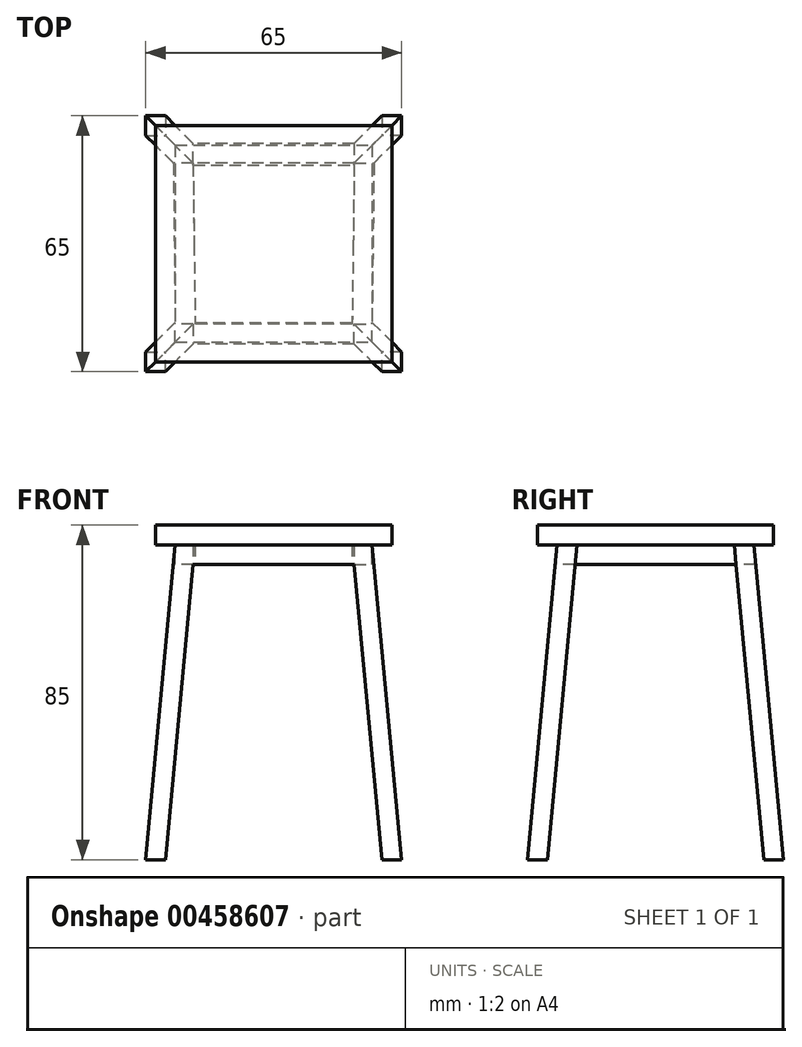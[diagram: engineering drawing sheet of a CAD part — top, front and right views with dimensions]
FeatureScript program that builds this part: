
annotation { "Feature Type Name" : "Feature", "Feature Type Description" : "" }
export const myFeature = defineFeature(function(context is Context, id is Id, definition is map)
    precondition{}
    {
        {
            var Q0;
            Q0=qCreatedBy(makeId("Top.planeOp"),FACE);
            var sketch = newSketch(context, id + "F0", { "sketchPlane" : qUnion([Q0])});
            skPoint(sketch, "E0.end.orphan", {"position": v(21.97, -20.2) * mm});
            skPoint(sketch, "E1.end.orphan", {"position": v(20, 29.8) * mm});
            skPoint(sketch, "E1.start.orphan", {"position": v(-30, 30) * mm});
            skLineSegment(sketch, "E2.bottom", {"start": v(-30, 30) * mm, "end": v(30, 30) * mm});
            skLineSegment(sketch, "E2.top", {"start": v(-30, -30) * mm, "end": v(30, -30) * mm});
            skLineSegment(sketch, "E2.left", {"start": v(-30, 30) * mm, "end": v(-30, -30) * mm});
            skLineSegment(sketch, "E2.right", {"start": v(30, 30) * mm, "end": v(30, -30) * mm});
            skPoint(sketch, "E2.middle", {"position": v(0, 0) * mm});
            skSolve(sketch);
        }
        {
            var Q0;
            Q0 = qSketchRegion(id + "F0", true);
            extrude(context, id + "F1", {"entities" : qUnion([Q0]), "depth" : 5 * mm});
        }
        {
            var Q0;
            Q0=makeQuery(id+"F1.opExtrude","CAP_FACE",FACE,{"disambiguationData":[OSD([sQuery(id+"F0.wireOp",EDGE,"E2.bottom"),sQuery(id+"F0.wireOp",EDGE,"E2.top"),sQuery(id+"F0.wireOp",EDGE,"E2.left"),sQuery(id+"F0.wireOp",EDGE,"E2.right")])],"isStart":true});
            var sketch = newSketch(context, id + "F2", { "sketchPlane" : qUnion([Q0])});
            skLineSegment(sketch, "E3.bottom", {"start": v(-25, 25) * mm, "end": v(25, 25) * mm, "construction": true});
            skLineSegment(sketch, "E3.top", {"start": v(-25, -25) * mm, "end": v(25, -25) * mm, "construction": true});
            skLineSegment(sketch, "E3.left", {"start": v(-25, 25) * mm, "end": v(-25, -25) * mm, "construction": true});
            skLineSegment(sketch, "E3.right", {"start": v(25, 25) * mm, "end": v(25, -25) * mm, "construction": true});
            skPoint(sketch, "E3.middle", {"position": v(0, 0) * mm});
            skLineSegment(sketch, "E4.bottom", {"start": v(-25, 25) * mm, "end": v(-20, 25) * mm});
            skLineSegment(sketch, "E4.top", {"start": v(-25, 20) * mm, "end": v(-20, 20) * mm});
            skLineSegment(sketch, "E4.left", {"start": v(-25, 25) * mm, "end": v(-25, 20) * mm});
            skLineSegment(sketch, "E4.right", {"start": v(-20, 25) * mm, "end": v(-20, 20) * mm});
            skSolve(sketch);
        }
        {
            var Q0;
            Q0=makeQuery(id+"F2.imprint","IMPRINT",FACE,{"disambiguationData":[TD([[makeQuery(id+"F2.imprint","IMPRINT",EDGE,{"derivedFrom":sQuery(id+"F2.wireOp",EDGE,"E4.bottom")}),1.0]])]});
            cPlane(context, id + "F3", {"entities" : qUnion([Q0]), "cplaneType" : CPlaneType.OFFSET, "offset" : 80 * mm, "width" : 150 * mm, "height" : 150 * mm});
        }
        {
            var Q0;
            Q0=qCreatedBy(id+"F3.planeOp",FACE);
            var sketch = newSketch(context, id + "F4", { "sketchPlane" : qUnion([Q0])});
            skLineSegment(sketch, "E5.bottom", {"start": v(-32.5, 32.5) * mm, "end": v(32.5, 32.5) * mm, "construction": true});
            skLineSegment(sketch, "E5.top", {"start": v(-32.5, -32.5) * mm, "end": v(32.5, -32.5) * mm, "construction": true});
            skLineSegment(sketch, "E5.left", {"start": v(-32.5, 32.5) * mm, "end": v(-32.5, -32.5) * mm, "construction": true});
            skLineSegment(sketch, "E5.right", {"start": v(32.5, 32.5) * mm, "end": v(32.5, -32.5) * mm, "construction": true});
            skPoint(sketch, "E5.middle", {"position": v(0, 0) * mm});
            skLineSegment(sketch, "E6.bottom", {"start": v(-32.5, 32.5) * mm, "end": v(-27.5, 32.5) * mm});
            skLineSegment(sketch, "E6.top", {"start": v(-32.5, 27.5) * mm, "end": v(-27.5, 27.5) * mm});
            skLineSegment(sketch, "E6.left", {"start": v(-32.5, 32.5) * mm, "end": v(-32.5, 27.5) * mm});
            skLineSegment(sketch, "E6.right", {"start": v(-27.5, 32.5) * mm, "end": v(-27.5, 27.5) * mm});
            skSolve(sketch);
        }
        {
            var Q1;
            Q1=makeQuery(id+"F2.imprint","IMPRINT",FACE,{"disambiguationData":[TD([[makeQuery(id+"F2.imprint","IMPRINT",EDGE,{"derivedFrom":sQuery(id+"F2.wireOp",EDGE,"E4.bottom")}),-1.0]])]});
            var Q2;
            Q2=makeQuery(id+"F4.imprint","IMPRINT",FACE,{"disambiguationData":[TD([[makeQuery(id+"F4.imprint","IMPRINT",EDGE,{"derivedFrom":sQuery(id+"F4.wireOp",EDGE,"E6.bottom")}),-1.0]])]});
            loft(context, id + "F5", {"sheetProfilesArray" : [{ "sheetProfileEntities" : qUnion([Q1]) }, { "sheetProfileEntities" : qUnion([Q2]) }]});
        }
        {
            var Q0;
            Q0=makeQuery(id+"F5.opLoft","SWEPT_BODY",BODY,{"disambiguationData":[OSD([makeQuery(id+"F2.imprint","IMPRINT",FACE,{"disambiguationData":[TD([[makeQuery(id+"F2.imprint","IMPRINT",EDGE,{"derivedFrom":sQuery(id+"F2.wireOp",EDGE,"E4.bottom")}),-1.0]])]}),makeQuery(id+"F4.imprint","IMPRINT",FACE,{"disambiguationData":[TD([[makeQuery(id+"F4.imprint","IMPRINT",EDGE,{"derivedFrom":sQuery(id+"F4.wireOp",EDGE,"E6.bottom")}),-1.0]])]})])]});
            var Q1;
            Q1=qCreatedBy(makeId("Right.planeOp"),FACE);
            mirror(context, id + "F6", {"entities" : qUnion([Q0]), "mirrorPlane" : qUnion([Q1])});
        }
        {
            var Q0;
            Q0=makeQuery(id+"F5.opLoft","SWEPT_BODY",BODY,{"disambiguationData":[OSD([makeQuery(id+"F2.imprint","IMPRINT",FACE,{"disambiguationData":[TD([[makeQuery(id+"F2.imprint","IMPRINT",EDGE,{"derivedFrom":sQuery(id+"F2.wireOp",EDGE,"E4.bottom")}),-1.0]])]}),makeQuery(id+"F4.imprint","IMPRINT",FACE,{"disambiguationData":[TD([[makeQuery(id+"F4.imprint","IMPRINT",EDGE,{"derivedFrom":sQuery(id+"F4.wireOp",EDGE,"E6.bottom")}),-1.0]])]})])]});
            var Q1;
            Q1=makeQuery(id+"F6.opPattern","COPY",BODY,{"derivedFrom":makeQuery(id+"F5.opLoft","SWEPT_BODY",BODY,{"disambiguationData":[OSD([makeQuery(id+"F2.imprint","IMPRINT",FACE,{"disambiguationData":[TD([[makeQuery(id+"F2.imprint","IMPRINT",EDGE,{"derivedFrom":sQuery(id+"F2.wireOp",EDGE,"E4.bottom")}),-1.0]])]}),makeQuery(id+"F4.imprint","IMPRINT",FACE,{"disambiguationData":[TD([[makeQuery(id+"F4.imprint","IMPRINT",EDGE,{"derivedFrom":sQuery(id+"F4.wireOp",EDGE,"E6.bottom")}),-1.0]])]})])]}),"instanceName":"1"});
            var Q2;
            Q2=qCreatedBy(makeId("Front.planeOp"),FACE);
            mirror(context, id + "F7", {"operationType" : NewBodyOperationType.ADD, "entities" : qUnion([Q0, Q1]), "mirrorPlane" : qUnion([Q2])});
        }
        {
            var Q0;
            Q0=makeQuery(id+"F5.opLoft","SWEPT_FACE",FACE,{"disambiguationData":[OSD([sQuery(id+"F2.wireOp",EDGE,"E4.bottom"),sQuery(id+"F2.wireOp",EDGE,"E4.top"),sQuery(id+"F2.wireOp",EDGE,"E4.right"),sQuery(id+"F4.wireOp",EDGE,"E6.bottom"),sQuery(id+"F4.wireOp",EDGE,"E6.top"),sQuery(id+"F4.wireOp",EDGE,"E6.right")])]});
            var sketch = newSketch(context, id + "F8", { "sketchPlane" : qUnion([Q0])});
            skLineSegment(sketch, "E7", {"start": v(-25, -1.87) * mm, "end": v(-20, -1.87) * mm});
            skLineSegment(sketch, "E8", {"start": v(-20, -1.87) * mm, "end": v(-20.46, -6.85) * mm});
            skLineSegment(sketch, "E9", {"start": v(-20.46, -6.85) * mm, "end": v(-25.46, -6.85) * mm});
            skLineSegment(sketch, "E10", {"start": v(-25.46, -6.85) * mm, "end": v(-25, -1.87) * mm});
            skSolve(sketch);
        }
        {
            var Q0;
            Q0=makeQuery(id+"F6.opPattern","COPY",FACE,{"derivedFrom":makeQuery(id+"F5.opLoft","SWEPT_FACE",FACE,{"disambiguationData":[OSD([sQuery(id+"F2.wireOp",EDGE,"E4.bottom"),sQuery(id+"F2.wireOp",EDGE,"E4.top"),sQuery(id+"F2.wireOp",EDGE,"E4.right"),sQuery(id+"F4.wireOp",EDGE,"E6.bottom"),sQuery(id+"F4.wireOp",EDGE,"E6.top"),sQuery(id+"F4.wireOp",EDGE,"E6.right")])]}),"instanceName":"1"});
            var sketch = newSketch(context, id + "F9", { "sketchPlane" : qUnion([Q0])});
            skLineSegment(sketch, "E11", {"start": v(20, -1.87) * mm, "end": v(25, -1.87) * mm});
            skLineSegment(sketch, "E12", {"start": v(25, -1.87) * mm, "end": v(25.46, -6.85) * mm});
            skLineSegment(sketch, "E13", {"start": v(25.46, -6.85) * mm, "end": v(20.46, -6.85) * mm});
            skLineSegment(sketch, "E14", {"start": v(20.46, -6.85) * mm, "end": v(20, -1.87) * mm});
            skSolve(sketch);
        }
        {
            var Q1;
            Q1=makeQuery(id+"F9.imprint","IMPRINT",FACE,{"disambiguationData":[TD([[makeQuery(id+"F9.imprint","IMPRINT",EDGE,{"derivedFrom":sQuery(id+"F9.wireOp",EDGE,"E11")}),-1.0]])]});
            var Q2;
            Q2=makeQuery(id+"F8.imprint","IMPRINT",FACE,{"disambiguationData":[TD([[makeQuery(id+"F8.imprint","IMPRINT",EDGE,{"derivedFrom":sQuery(id+"F8.wireOp",EDGE,"E7")}),1.0]])]});
            loft(context, id + "F10", {"sheetProfilesArray" : [{ "sheetProfileEntities" : qUnion([Q1]) }, { "sheetProfileEntities" : qUnion([Q2]) }]});
        }
        {
            var Q0;
            Q0=makeQuery(id+"F10.opLoft","SWEPT_BODY",BODY,{"disambiguationData":[OSD([makeQuery(id+"F8.imprint","IMPRINT",FACE,{"disambiguationData":[TD([[makeQuery(id+"F8.imprint","IMPRINT",EDGE,{"derivedFrom":sQuery(id+"F8.wireOp",EDGE,"E7")}),1.0]])]}),makeQuery(id+"F9.imprint","IMPRINT",FACE,{"disambiguationData":[TD([[makeQuery(id+"F9.imprint","IMPRINT",EDGE,{"derivedFrom":sQuery(id+"F9.wireOp",EDGE,"E11")}),-1.0]])]})])]});
            var Q1;
            Q1=qCreatedBy(makeId("Front.planeOp"),FACE);
            mirror(context, id + "F11", {"operationType" : NewBodyOperationType.ADD, "entities" : qUnion([Q0]), "mirrorPlane" : qUnion([Q1])});
        }
        {
            var Q0;
            {var subQ0=sQuery(id+"F4.wireOp",EDGE,"E6.right");var subQ1=sQuery(id+"F4.wireOp",EDGE,"E6.top");var subQ2=sQuery(id+"F2.wireOp",EDGE,"E4.right");var subQ3=sQuery(id+"F2.wireOp",EDGE,"E4.top");var subQ4=makeQuery(id+"F5.opLoft","SWEPT_FACE",FACE,{"disambiguationData":[OSD([subQ3,sQuery(id+"F2.wireOp",EDGE,"E4.left"),subQ2,subQ1,sQuery(id+"F4.wireOp",EDGE,"E6.left"),subQ0])]});Q0=makeQuery(id+"F11.boolean.opBoolean","MERGE",FACE,{"derivedFrom":[makeQuery(id+"F7.opPattern","COPY",FACE,{"derivedFrom":subQ4,"instanceName":"1"}),makeQuery(id+"F7.opPattern","COPY",FACE,{"derivedFrom":makeQuery(id+"F6.opPattern","COPY",FACE,{"derivedFrom":subQ4,"instanceName":"1"}),"instanceName":"1"}),makeQuery(id+"F11.opPattern","COPY",FACE,{"derivedFrom":makeQuery(id+"F10.opLoft","SWEPT_FACE",FACE,{"disambiguationData":[OSD([subQ3,subQ2,subQ1,subQ0,sQuery(id+"F8.wireOp",EDGE,"E7"),sQuery(id+"F8.wireOp",EDGE,"E8"),sQuery(id+"F8.wireOp",EDGE,"E9"),sQuery(id+"F9.wireOp",EDGE,"E11"),sQuery(id+"F9.wireOp",EDGE,"E13"),sQuery(id+"F9.wireOp",EDGE,"E14")])]}),"instanceName":"1"})]});}
            var sketch = newSketch(context, id + "F12", { "sketchPlane" : qUnion([Q0])});
            skLineSegment(sketch, "E15", {"start": v(-20.46, -6.85) * mm, "end": v(-25.46, -6.85) * mm});
            skLineSegment(sketch, "E16", {"start": v(-25.46, -6.85) * mm, "end": v(-25, -1.87) * mm});
            skLineSegment(sketch, "E17", {"start": v(-25, -1.87) * mm, "end": v(-20.46, -1.87) * mm});
            skLineSegment(sketch, "E18", {"start": v(-20.46, -1.87) * mm, "end": v(-20.46, -6.85) * mm});
            skSolve(sketch);
        }
        {
            var Q0;
            {var subQ0=sQuery(id+"F4.wireOp",EDGE,"E6.right");var subQ1=sQuery(id+"F4.wireOp",EDGE,"E6.top");var subQ2=sQuery(id+"F2.wireOp",EDGE,"E4.right");var subQ3=sQuery(id+"F2.wireOp",EDGE,"E4.top");var subQ4=makeQuery(id+"F5.opLoft","SWEPT_FACE",FACE,{"disambiguationData":[OSD([subQ3,sQuery(id+"F2.wireOp",EDGE,"E4.left"),subQ2,subQ1,sQuery(id+"F4.wireOp",EDGE,"E6.left"),subQ0])]});Q0=makeQuery(id+"F11.boolean.opBoolean","MERGE",FACE,{"derivedFrom":[subQ4,makeQuery(id+"F6.opPattern","COPY",FACE,{"derivedFrom":subQ4,"instanceName":"1"}),makeQuery(id+"F10.opLoft","SWEPT_FACE",FACE,{"disambiguationData":[OSD([subQ3,subQ2,subQ1,subQ0,sQuery(id+"F8.wireOp",EDGE,"E7"),sQuery(id+"F8.wireOp",EDGE,"E8"),sQuery(id+"F8.wireOp",EDGE,"E9"),sQuery(id+"F9.wireOp",EDGE,"E11"),sQuery(id+"F9.wireOp",EDGE,"E13"),sQuery(id+"F9.wireOp",EDGE,"E14")])]})]});}
            var sketch = newSketch(context, id + "F13", { "sketchPlane" : qUnion([Q0])});
            skLineSegment(sketch, "E19", {"start": v(25, -1.87) * mm, "end": v(19.95, -1.87) * mm});
            skLineSegment(sketch, "E20", {"start": v(19.95, -1.87) * mm, "end": v(19.95, -6.85) * mm});
            skLineSegment(sketch, "E21", {"start": v(19.95, -6.85) * mm, "end": v(25, -6.85) * mm});
            skLineSegment(sketch, "E22", {"start": v(25, -6.85) * mm, "end": v(25, -1.87) * mm});
            skSolve(sketch);
        }
        {
            var Q1;
            Q1=makeQuery(id+"F12.imprint","IMPRINT",FACE,{"disambiguationData":[TD([[makeQuery(id+"F12.imprint","IMPRINT",EDGE,{"derivedFrom":sQuery(id+"F12.wireOp",EDGE,"E15")}),-1.0]])]});
            var Q2;
            Q2=makeQuery(id+"F13.imprint","IMPRINT",FACE,{"disambiguationData":[TD([[makeQuery(id+"F13.imprint","IMPRINT",EDGE,{"derivedFrom":sQuery(id+"F13.wireOp",EDGE,"E19")}),1.0]])]});
            loft(context, id + "F14", {"sheetProfilesArray" : [{ "sheetProfileEntities" : qUnion([Q1]) }, { "sheetProfileEntities" : qUnion([Q2]) }]});
        }
        {
            var Q0;
            Q0=makeQuery(id+"F14.opLoft","SWEPT_BODY",BODY,{"disambiguationData":[OSD([makeQuery(id+"F12.imprint","IMPRINT",FACE,{"disambiguationData":[TD([[makeQuery(id+"F12.imprint","IMPRINT",EDGE,{"derivedFrom":sQuery(id+"F12.wireOp",EDGE,"E15")}),-1.0]])]}),makeQuery(id+"F13.imprint","IMPRINT",FACE,{"disambiguationData":[TD([[makeQuery(id+"F13.imprint","IMPRINT",EDGE,{"derivedFrom":sQuery(id+"F13.wireOp",EDGE,"E19")}),1.0]])]})])]});
            var Q1;
            Q1=qCreatedBy(makeId("Right.planeOp"),FACE);
            mirror(context, id + "F15", {"operationType" : NewBodyOperationType.ADD, "entities" : qUnion([Q0]), "mirrorPlane" : qUnion([Q1])});
        }
    });
